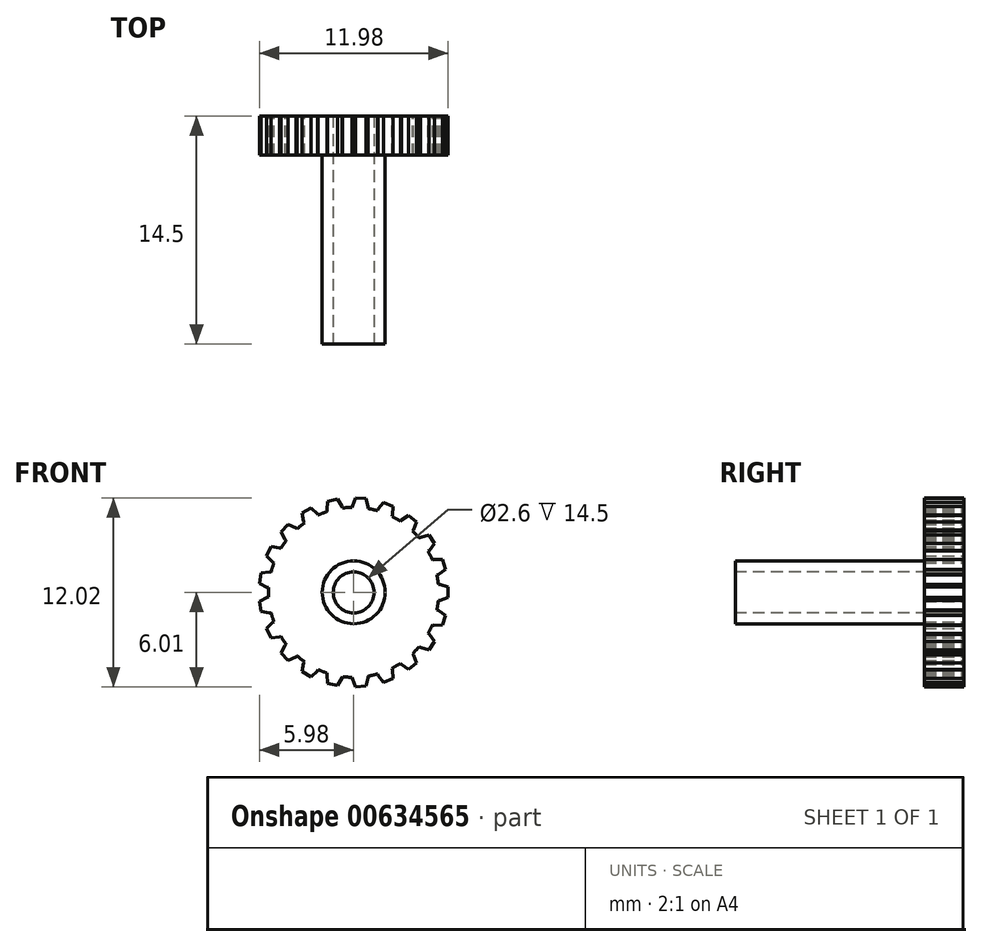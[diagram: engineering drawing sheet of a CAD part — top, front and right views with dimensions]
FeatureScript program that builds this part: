
annotation { "Feature Type Name" : "Feature", "Feature Type Description" : "" }
export const myFeature = defineFeature(function(context is Context, id is Id, definition is map)
    precondition{}
    {
        {
            var Q0;
            Q0=qCreatedBy(makeId("Front.planeOp"),FACE);
            var sketch = newSketch(context, id + "F0", { "sketchPlane" : qUnion([Q0])});
            skCircle(sketch, "E0", {"center": v(0, 0) * mm, "radius": 5.4 * mm});
            skLineSegment(sketch, "E1", {"start": v(0, 0) * mm, "end": v(5.4, 0) * mm, "construction": true});
            skLineSegment(sketch, "E2", {"start": v(5.4, 0) * mm, "end": v(6, 0) * mm, "construction": true});
            skLineSegment(sketch, "E3", {"start": v(6, 0) * mm, "end": v(6, 0.33) * mm});
            skLineSegment(sketch, "E4", {"start": v(5.38, 0.5) * mm, "end": v(5.48, 0.5) * mm});
            skLineSegment(sketch, "E5", {"start": v(5.48, 0.5) * mm, "end": v(6, 0.33) * mm});
            skLineSegment(sketch, "E6.MirrorCS", {"start": v(5.48, -0.5) * mm, "end": v(6, -0.33) * mm});
            skLineSegment(sketch, "E7.MirrorCS", {"start": v(6, 0) * mm, "end": v(6, -0.33) * mm});
            skLineSegment(sketch, "E8.MirrorCS", {"start": v(5.38, -0.5) * mm, "end": v(5.48, -0.5) * mm});
            skLineSegment(sketch, "E9.1.0", {"start": v(5, 2.06) * mm, "end": v(5.09, 2.1) * mm});
            skLineSegment(sketch, "E9.1.1", {"start": v(5.09, 2.1) * mm, "end": v(5.64, 2.08) * mm});
            skLineSegment(sketch, "E9.1.2", {"start": v(5.73, 1.77) * mm, "end": v(5.64, 2.08) * mm});
            skLineSegment(sketch, "E9.1.3", {"start": v(5.73, 1.77) * mm, "end": v(5.83, 1.45) * mm});
            skLineSegment(sketch, "E9.1.4", {"start": v(5.38, 1.14) * mm, "end": v(5.83, 1.45) * mm});
            skLineSegment(sketch, "E9.1.5", {"start": v(5.29, 1.1) * mm, "end": v(5.38, 1.14) * mm});
            skLineSegment(sketch, "E9.2.0", {"start": v(4.16, 3.44) * mm, "end": v(4.24, 3.5) * mm});
            skLineSegment(sketch, "E9.2.1", {"start": v(4.24, 3.5) * mm, "end": v(4.77, 3.65) * mm});
            skLineSegment(sketch, "E9.2.2", {"start": v(4.96, 3.38) * mm, "end": v(4.77, 3.65) * mm});
            skLineSegment(sketch, "E9.2.3", {"start": v(4.96, 3.38) * mm, "end": v(5.14, 3.1) * mm});
            skLineSegment(sketch, "E9.2.4", {"start": v(4.8, 2.67) * mm, "end": v(5.14, 3.1) * mm});
            skLineSegment(sketch, "E9.2.5", {"start": v(4.72, 2.62) * mm, "end": v(4.8, 2.67) * mm});
            skLineSegment(sketch, "E9.3.0", {"start": v(2.96, 4.52) * mm, "end": v(3.02, 4.6) * mm});
            skLineSegment(sketch, "E9.3.1", {"start": v(3.02, 4.6) * mm, "end": v(3.48, 4.9) * mm});
            skLineSegment(sketch, "E9.3.2", {"start": v(3.74, 4.7) * mm, "end": v(3.48, 4.9) * mm});
            skLineSegment(sketch, "E9.3.3", {"start": v(3.74, 4.7) * mm, "end": v(4, 4.49) * mm});
            skLineSegment(sketch, "E9.3.4", {"start": v(3.8, 3.97) * mm, "end": v(4, 4.49) * mm});
            skLineSegment(sketch, "E9.3.5", {"start": v(3.74, 3.9) * mm, "end": v(3.8, 3.97) * mm});
            skLineSegment(sketch, "E9.4.0", {"start": v(1.5, 5.19) * mm, "end": v(1.54, 5.28) * mm});
            skLineSegment(sketch, "E9.4.1", {"start": v(1.54, 5.28) * mm, "end": v(1.88, 5.7) * mm});
            skLineSegment(sketch, "E9.4.2", {"start": v(2.2, 5.59) * mm, "end": v(1.88, 5.7) * mm});
            skLineSegment(sketch, "E9.4.3", {"start": v(2.2, 5.59) * mm, "end": v(2.5, 5.46) * mm});
            skLineSegment(sketch, "E9.4.4", {"start": v(2.47, 4.92) * mm, "end": v(2.5, 5.46) * mm});
            skLineSegment(sketch, "E9.4.5", {"start": v(2.43, 4.82) * mm, "end": v(2.47, 4.92) * mm});
            skLineSegment(sketch, "E9.5.0", {"start": v(-0.1, 5.4) * mm, "end": v(-0.09, 5.5) * mm});
            skLineSegment(sketch, "E9.5.1", {"start": v(-0.09, 5.5) * mm, "end": v(0.12, 6) * mm});
            skLineSegment(sketch, "E9.5.2", {"start": v(0.45, 5.98) * mm, "end": v(0.12, 6) * mm});
            skLineSegment(sketch, "E9.5.3", {"start": v(0.45, 5.98) * mm, "end": v(0.78, 5.96) * mm});
            skLineSegment(sketch, "E9.5.4", {"start": v(0.9, 5.42) * mm, "end": v(0.78, 5.96) * mm});
            skLineSegment(sketch, "E9.5.5", {"start": v(0.9, 5.32) * mm, "end": v(0.9, 5.42) * mm});
            skLineSegment(sketch, "E9.6.0", {"start": v(-1.68, 5.13) * mm, "end": v(-1.7, 5.23) * mm});
            skLineSegment(sketch, "E9.6.1", {"start": v(-1.7, 5.23) * mm, "end": v(-1.66, 5.78) * mm});
            skLineSegment(sketch, "E9.6.2", {"start": v(-1.34, 5.85) * mm, "end": v(-1.66, 5.78) * mm});
            skLineSegment(sketch, "E9.6.3", {"start": v(-1.34, 5.85) * mm, "end": v(-1.01, 5.92) * mm});
            skLineSegment(sketch, "E9.6.4", {"start": v(-0.73, 5.45) * mm, "end": v(-1.01, 5.92) * mm});
            skLineSegment(sketch, "E9.6.5", {"start": v(-0.7, 5.35) * mm, "end": v(-0.73, 5.45) * mm});
            skLineSegment(sketch, "E9.7.0", {"start": v(-3.12, 4.4) * mm, "end": v(-3.17, 4.5) * mm});
            skLineSegment(sketch, "E9.7.1", {"start": v(-3.17, 4.5) * mm, "end": v(-3.29, 5.03) * mm});
            skLineSegment(sketch, "E9.7.2", {"start": v(-3, 5.2) * mm, "end": v(-3.29, 5.03) * mm});
            skLineSegment(sketch, "E9.7.3", {"start": v(-3, 5.2) * mm, "end": v(-2.71, 5.36) * mm});
            skLineSegment(sketch, "E9.7.4", {"start": v(-2.3, 5) * mm, "end": v(-2.71, 5.36) * mm});
            skLineSegment(sketch, "E9.7.5", {"start": v(-2.26, 4.9) * mm, "end": v(-2.3, 5) * mm});
            skLineSegment(sketch, "E9.8.0", {"start": v(-4.28, 3.3) * mm, "end": v(-4.35, 3.36) * mm});
            skLineSegment(sketch, "E9.8.1", {"start": v(-4.35, 3.36) * mm, "end": v(-4.62, 3.84) * mm});
            skLineSegment(sketch, "E9.8.2", {"start": v(-4.4, 4.08) * mm, "end": v(-4.62, 3.84) * mm});
            skLineSegment(sketch, "E9.8.3", {"start": v(-4.4, 4.08) * mm, "end": v(-4.17, 4.32) * mm});
            skLineSegment(sketch, "E9.8.4", {"start": v(-3.67, 4.1) * mm, "end": v(-4.17, 4.32) * mm});
            skLineSegment(sketch, "E9.8.5", {"start": v(-3.6, 4.02) * mm, "end": v(-3.67, 4.1) * mm});
            skLineSegment(sketch, "E9.9.0", {"start": v(-5.06, 1.88) * mm, "end": v(-5.15, 1.93) * mm});
            skLineSegment(sketch, "E9.9.1", {"start": v(-5.15, 1.93) * mm, "end": v(-5.55, 2.3) * mm});
            skLineSegment(sketch, "E9.9.2", {"start": v(-5.4, 2.6) * mm, "end": v(-5.55, 2.3) * mm});
            skLineSegment(sketch, "E9.9.3", {"start": v(-5.4, 2.6) * mm, "end": v(-5.26, 2.9) * mm});
            skLineSegment(sketch, "E9.9.4", {"start": v(-4.72, 2.83) * mm, "end": v(-5.26, 2.9) * mm});
            skLineSegment(sketch, "E9.9.5", {"start": v(-4.63, 2.78) * mm, "end": v(-4.72, 2.83) * mm});
            skLineSegment(sketch, "E9.10.0", {"start": v(-5.4, 0.3) * mm, "end": v(-5.5, 0.32) * mm});
            skLineSegment(sketch, "E9.10.1", {"start": v(-5.5, 0.32) * mm, "end": v(-5.98, 0.57) * mm});
            skLineSegment(sketch, "E9.10.2", {"start": v(-5.93, 0.9) * mm, "end": v(-5.98, 0.57) * mm});
            skLineSegment(sketch, "E9.10.3", {"start": v(-5.93, 0.9) * mm, "end": v(-5.88, 1.22) * mm});
            skLineSegment(sketch, "E9.10.4", {"start": v(-5.34, 1.31) * mm, "end": v(-5.88, 1.22) * mm});
            skLineSegment(sketch, "E9.10.5", {"start": v(-5.24, 1.3) * mm, "end": v(-5.34, 1.31) * mm});
            skLineSegment(sketch, "E9.11.0", {"start": v(-5.24, -1.3) * mm, "end": v(-5.34, -1.31) * mm});
            skLineSegment(sketch, "E9.11.1", {"start": v(-5.34, -1.31) * mm, "end": v(-5.88, -1.22) * mm});
            skLineSegment(sketch, "E9.11.2", {"start": v(-5.93, -0.9) * mm, "end": v(-5.88, -1.22) * mm});
            skLineSegment(sketch, "E9.11.3", {"start": v(-5.93, -0.9) * mm, "end": v(-5.98, -0.57) * mm});
            skLineSegment(sketch, "E9.11.4", {"start": v(-5.5, -0.32) * mm, "end": v(-5.98, -0.57) * mm});
            skLineSegment(sketch, "E9.11.5", {"start": v(-5.4, -0.3) * mm, "end": v(-5.5, -0.32) * mm});
            skLineSegment(sketch, "E9.12.0", {"start": v(-4.63, -2.78) * mm, "end": v(-4.72, -2.83) * mm});
            skLineSegment(sketch, "E9.12.1", {"start": v(-4.72, -2.83) * mm, "end": v(-5.26, -2.9) * mm});
            skLineSegment(sketch, "E9.12.2", {"start": v(-5.4, -2.6) * mm, "end": v(-5.26, -2.9) * mm});
            skLineSegment(sketch, "E9.12.3", {"start": v(-5.4, -2.6) * mm, "end": v(-5.55, -2.3) * mm});
            skLineSegment(sketch, "E9.12.4", {"start": v(-5.15, -1.93) * mm, "end": v(-5.55, -2.3) * mm});
            skLineSegment(sketch, "E9.12.5", {"start": v(-5.06, -1.88) * mm, "end": v(-5.15, -1.93) * mm});
            skLineSegment(sketch, "E9.13.0", {"start": v(-3.6, -4.02) * mm, "end": v(-3.67, -4.1) * mm});
            skLineSegment(sketch, "E9.13.1", {"start": v(-3.67, -4.1) * mm, "end": v(-4.17, -4.32) * mm});
            skLineSegment(sketch, "E9.13.2", {"start": v(-4.4, -4.08) * mm, "end": v(-4.17, -4.32) * mm});
            skLineSegment(sketch, "E9.13.3", {"start": v(-4.4, -4.08) * mm, "end": v(-4.62, -3.84) * mm});
            skLineSegment(sketch, "E9.13.4", {"start": v(-4.35, -3.36) * mm, "end": v(-4.62, -3.84) * mm});
            skLineSegment(sketch, "E9.13.5", {"start": v(-4.28, -3.3) * mm, "end": v(-4.35, -3.36) * mm});
            skLineSegment(sketch, "E9.14.0", {"start": v(-2.26, -4.9) * mm, "end": v(-2.3, -5) * mm});
            skLineSegment(sketch, "E9.14.1", {"start": v(-2.3, -5) * mm, "end": v(-2.71, -5.36) * mm});
            skLineSegment(sketch, "E9.14.2", {"start": v(-3, -5.2) * mm, "end": v(-2.71, -5.36) * mm});
            skLineSegment(sketch, "E9.14.3", {"start": v(-3, -5.2) * mm, "end": v(-3.29, -5.03) * mm});
            skLineSegment(sketch, "E9.14.4", {"start": v(-3.17, -4.5) * mm, "end": v(-3.29, -5.03) * mm});
            skLineSegment(sketch, "E9.14.5", {"start": v(-3.12, -4.4) * mm, "end": v(-3.17, -4.5) * mm});
            skLineSegment(sketch, "E9.15.0", {"start": v(-0.7, -5.35) * mm, "end": v(-0.73, -5.45) * mm});
            skLineSegment(sketch, "E9.15.1", {"start": v(-0.73, -5.45) * mm, "end": v(-1.01, -5.92) * mm});
            skLineSegment(sketch, "E9.15.2", {"start": v(-1.34, -5.85) * mm, "end": v(-1.01, -5.92) * mm});
            skLineSegment(sketch, "E9.15.3", {"start": v(-1.34, -5.85) * mm, "end": v(-1.66, -5.78) * mm});
            skLineSegment(sketch, "E9.15.4", {"start": v(-1.7, -5.23) * mm, "end": v(-1.66, -5.78) * mm});
            skLineSegment(sketch, "E9.15.5", {"start": v(-1.68, -5.13) * mm, "end": v(-1.7, -5.23) * mm});
            skLineSegment(sketch, "E9.16.0", {"start": v(0.9, -5.32) * mm, "end": v(0.9, -5.42) * mm});
            skLineSegment(sketch, "E9.16.1", {"start": v(0.9, -5.42) * mm, "end": v(0.78, -5.96) * mm});
            skLineSegment(sketch, "E9.16.2", {"start": v(0.45, -5.98) * mm, "end": v(0.78, -5.96) * mm});
            skLineSegment(sketch, "E9.16.3", {"start": v(0.45, -5.98) * mm, "end": v(0.12, -6) * mm});
            skLineSegment(sketch, "E9.16.4", {"start": v(-0.09, -5.5) * mm, "end": v(0.12, -6) * mm});
            skLineSegment(sketch, "E9.16.5", {"start": v(-0.1, -5.4) * mm, "end": v(-0.09, -5.5) * mm});
            skLineSegment(sketch, "E9.17.0", {"start": v(2.43, -4.82) * mm, "end": v(2.47, -4.92) * mm});
            skLineSegment(sketch, "E9.17.1", {"start": v(2.47, -4.92) * mm, "end": v(2.5, -5.46) * mm});
            skLineSegment(sketch, "E9.17.2", {"start": v(2.2, -5.59) * mm, "end": v(2.5, -5.46) * mm});
            skLineSegment(sketch, "E9.17.3", {"start": v(2.2, -5.59) * mm, "end": v(1.88, -5.7) * mm});
            skLineSegment(sketch, "E9.17.4", {"start": v(1.54, -5.28) * mm, "end": v(1.88, -5.7) * mm});
            skLineSegment(sketch, "E9.17.5", {"start": v(1.5, -5.19) * mm, "end": v(1.54, -5.28) * mm});
            skLineSegment(sketch, "E9.18.0", {"start": v(3.74, -3.9) * mm, "end": v(3.8, -3.97) * mm});
            skLineSegment(sketch, "E9.18.1", {"start": v(3.8, -3.97) * mm, "end": v(4, -4.49) * mm});
            skLineSegment(sketch, "E9.18.2", {"start": v(3.74, -4.7) * mm, "end": v(4, -4.49) * mm});
            skLineSegment(sketch, "E9.18.3", {"start": v(3.74, -4.7) * mm, "end": v(3.48, -4.9) * mm});
            skLineSegment(sketch, "E9.18.4", {"start": v(3.02, -4.6) * mm, "end": v(3.48, -4.9) * mm});
            skLineSegment(sketch, "E9.18.5", {"start": v(2.96, -4.52) * mm, "end": v(3.02, -4.6) * mm});
            skLineSegment(sketch, "E9.19.0", {"start": v(4.72, -2.62) * mm, "end": v(4.8, -2.67) * mm});
            skLineSegment(sketch, "E9.19.1", {"start": v(4.8, -2.67) * mm, "end": v(5.14, -3.1) * mm});
            skLineSegment(sketch, "E9.19.2", {"start": v(4.96, -3.38) * mm, "end": v(5.14, -3.1) * mm});
            skLineSegment(sketch, "E9.19.3", {"start": v(4.96, -3.38) * mm, "end": v(4.77, -3.65) * mm});
            skLineSegment(sketch, "E9.19.4", {"start": v(4.24, -3.5) * mm, "end": v(4.77, -3.65) * mm});
            skLineSegment(sketch, "E9.19.5", {"start": v(4.16, -3.44) * mm, "end": v(4.24, -3.5) * mm});
            skLineSegment(sketch, "E9.20.0", {"start": v(5.29, -1.1) * mm, "end": v(5.38, -1.14) * mm});
            skLineSegment(sketch, "E9.20.1", {"start": v(5.38, -1.14) * mm, "end": v(5.83, -1.45) * mm});
            skLineSegment(sketch, "E9.20.2", {"start": v(5.73, -1.77) * mm, "end": v(5.83, -1.45) * mm});
            skLineSegment(sketch, "E9.20.3", {"start": v(5.73, -1.77) * mm, "end": v(5.64, -2.08) * mm});
            skLineSegment(sketch, "E9.20.4", {"start": v(5.09, -2.1) * mm, "end": v(5.64, -2.08) * mm});
            skLineSegment(sketch, "E9.20.5", {"start": v(5, -2.06) * mm, "end": v(5.09, -2.1) * mm});
            skSolve(sketch);
        }
        {
            var Q0;
            Q0=qSketchRegion(id+"F0",true);
            extrude(context, id + "F1", {"entities" : qUnion([Q0]), "depth" : 2.5 * mm, "offsetDistance" : 25.4 * mm});
        }
        {
            var Q0;
            Q0=makeQuery(id+"F1.opExtrude","CAP_FACE",FACE,{"disambiguationData":[OSD([sQuery(id+"F0.wireOp",EDGE,"E0"),sQuery(id+"F0.wireOp",EDGE,"E3"),sQuery(id+"F0.wireOp",EDGE,"E4"),sQuery(id+"F0.wireOp",EDGE,"E5"),sQuery(id+"F0.wireOp",EDGE,"E6.MirrorCS"),sQuery(id+"F0.wireOp",EDGE,"E7.MirrorCS"),sQuery(id+"F0.wireOp",EDGE,"E8.MirrorCS"),sQuery(id+"F0.wireOp",EDGE,"E9.1.0"),sQuery(id+"F0.wireOp",EDGE,"E9.1.1"),sQuery(id+"F0.wireOp",EDGE,"E9.1.2"),sQuery(id+"F0.wireOp",EDGE,"E9.1.3"),sQuery(id+"F0.wireOp",EDGE,"E9.1.4"),sQuery(id+"F0.wireOp",EDGE,"E9.1.5"),sQuery(id+"F0.wireOp",EDGE,"E9.2.0"),sQuery(id+"F0.wireOp",EDGE,"E9.2.1"),sQuery(id+"F0.wireOp",EDGE,"E9.2.2"),sQuery(id+"F0.wireOp",EDGE,"E9.2.3"),sQuery(id+"F0.wireOp",EDGE,"E9.2.4"),sQuery(id+"F0.wireOp",EDGE,"E9.2.5"),sQuery(id+"F0.wireOp",EDGE,"E9.3.0"),sQuery(id+"F0.wireOp",EDGE,"E9.3.1"),sQuery(id+"F0.wireOp",EDGE,"E9.3.2"),sQuery(id+"F0.wireOp",EDGE,"E9.3.3"),sQuery(id+"F0.wireOp",EDGE,"E9.3.4"),sQuery(id+"F0.wireOp",EDGE,"E9.3.5"),sQuery(id+"F0.wireOp",EDGE,"E9.4.0"),sQuery(id+"F0.wireOp",EDGE,"E9.4.1"),sQuery(id+"F0.wireOp",EDGE,"E9.4.2"),sQuery(id+"F0.wireOp",EDGE,"E9.4.3"),sQuery(id+"F0.wireOp",EDGE,"E9.4.4"),sQuery(id+"F0.wireOp",EDGE,"E9.4.5"),sQuery(id+"F0.wireOp",EDGE,"E9.5.0"),sQuery(id+"F0.wireOp",EDGE,"E9.5.1"),sQuery(id+"F0.wireOp",EDGE,"E9.5.2"),sQuery(id+"F0.wireOp",EDGE,"E9.5.3"),sQuery(id+"F0.wireOp",EDGE,"E9.5.4"),sQuery(id+"F0.wireOp",EDGE,"E9.5.5"),sQuery(id+"F0.wireOp",EDGE,"E9.6.0"),sQuery(id+"F0.wireOp",EDGE,"E9.6.1"),sQuery(id+"F0.wireOp",EDGE,"E9.6.2"),sQuery(id+"F0.wireOp",EDGE,"E9.6.3"),sQuery(id+"F0.wireOp",EDGE,"E9.6.4"),sQuery(id+"F0.wireOp",EDGE,"E9.6.5"),sQuery(id+"F0.wireOp",EDGE,"E9.7.0"),sQuery(id+"F0.wireOp",EDGE,"E9.7.1"),sQuery(id+"F0.wireOp",EDGE,"E9.7.2"),sQuery(id+"F0.wireOp",EDGE,"E9.7.3"),sQuery(id+"F0.wireOp",EDGE,"E9.7.4"),sQuery(id+"F0.wireOp",EDGE,"E9.7.5"),sQuery(id+"F0.wireOp",EDGE,"E9.8.0"),sQuery(id+"F0.wireOp",EDGE,"E9.8.1"),sQuery(id+"F0.wireOp",EDGE,"E9.8.2"),sQuery(id+"F0.wireOp",EDGE,"E9.8.3"),sQuery(id+"F0.wireOp",EDGE,"E9.8.4"),sQuery(id+"F0.wireOp",EDGE,"E9.8.5"),sQuery(id+"F0.wireOp",EDGE,"E9.9.0"),sQuery(id+"F0.wireOp",EDGE,"E9.9.1"),sQuery(id+"F0.wireOp",EDGE,"E9.9.2"),sQuery(id+"F0.wireOp",EDGE,"E9.9.3"),sQuery(id+"F0.wireOp",EDGE,"E9.9.4"),sQuery(id+"F0.wireOp",EDGE,"E9.9.5"),sQuery(id+"F0.wireOp",EDGE,"E9.10.0"),sQuery(id+"F0.wireOp",EDGE,"E9.10.1"),sQuery(id+"F0.wireOp",EDGE,"E9.10.2"),sQuery(id+"F0.wireOp",EDGE,"E9.10.3"),sQuery(id+"F0.wireOp",EDGE,"E9.10.4"),sQuery(id+"F0.wireOp",EDGE,"E9.10.5"),sQuery(id+"F0.wireOp",EDGE,"E9.11.0"),sQuery(id+"F0.wireOp",EDGE,"E9.11.1"),sQuery(id+"F0.wireOp",EDGE,"E9.11.2"),sQuery(id+"F0.wireOp",EDGE,"E9.11.3"),sQuery(id+"F0.wireOp",EDGE,"E9.11.4"),sQuery(id+"F0.wireOp",EDGE,"E9.11.5"),sQuery(id+"F0.wireOp",EDGE,"E9.12.0"),sQuery(id+"F0.wireOp",EDGE,"E9.12.1"),sQuery(id+"F0.wireOp",EDGE,"E9.12.2"),sQuery(id+"F0.wireOp",EDGE,"E9.12.3"),sQuery(id+"F0.wireOp",EDGE,"E9.12.4"),sQuery(id+"F0.wireOp",EDGE,"E9.12.5"),sQuery(id+"F0.wireOp",EDGE,"E9.13.0"),sQuery(id+"F0.wireOp",EDGE,"E9.13.1"),sQuery(id+"F0.wireOp",EDGE,"E9.13.2"),sQuery(id+"F0.wireOp",EDGE,"E9.13.3"),sQuery(id+"F0.wireOp",EDGE,"E9.13.4"),sQuery(id+"F0.wireOp",EDGE,"E9.13.5"),sQuery(id+"F0.wireOp",EDGE,"E9.14.0"),sQuery(id+"F0.wireOp",EDGE,"E9.14.1"),sQuery(id+"F0.wireOp",EDGE,"E9.14.2"),sQuery(id+"F0.wireOp",EDGE,"E9.14.3"),sQuery(id+"F0.wireOp",EDGE,"E9.14.4"),sQuery(id+"F0.wireOp",EDGE,"E9.14.5"),sQuery(id+"F0.wireOp",EDGE,"E9.15.0"),sQuery(id+"F0.wireOp",EDGE,"E9.15.1"),sQuery(id+"F0.wireOp",EDGE,"E9.15.2"),sQuery(id+"F0.wireOp",EDGE,"E9.15.3"),sQuery(id+"F0.wireOp",EDGE,"E9.15.4"),sQuery(id+"F0.wireOp",EDGE,"E9.15.5"),sQuery(id+"F0.wireOp",EDGE,"E9.16.0"),sQuery(id+"F0.wireOp",EDGE,"E9.16.1"),sQuery(id+"F0.wireOp",EDGE,"E9.16.2"),sQuery(id+"F0.wireOp",EDGE,"E9.16.3"),sQuery(id+"F0.wireOp",EDGE,"E9.16.4"),sQuery(id+"F0.wireOp",EDGE,"E9.16.5"),sQuery(id+"F0.wireOp",EDGE,"E9.17.0"),sQuery(id+"F0.wireOp",EDGE,"E9.17.1"),sQuery(id+"F0.wireOp",EDGE,"E9.17.2"),sQuery(id+"F0.wireOp",EDGE,"E9.17.3"),sQuery(id+"F0.wireOp",EDGE,"E9.17.4"),sQuery(id+"F0.wireOp",EDGE,"E9.17.5"),sQuery(id+"F0.wireOp",EDGE,"E9.18.0"),sQuery(id+"F0.wireOp",EDGE,"E9.18.1"),sQuery(id+"F0.wireOp",EDGE,"E9.18.2"),sQuery(id+"F0.wireOp",EDGE,"E9.18.3"),sQuery(id+"F0.wireOp",EDGE,"E9.18.4"),sQuery(id+"F0.wireOp",EDGE,"E9.18.5"),sQuery(id+"F0.wireOp",EDGE,"E9.19.0"),sQuery(id+"F0.wireOp",EDGE,"E9.19.1"),sQuery(id+"F0.wireOp",EDGE,"E9.19.2"),sQuery(id+"F0.wireOp",EDGE,"E9.19.3"),sQuery(id+"F0.wireOp",EDGE,"E9.19.4"),sQuery(id+"F0.wireOp",EDGE,"E9.19.5"),sQuery(id+"F0.wireOp",EDGE,"E9.20.0"),sQuery(id+"F0.wireOp",EDGE,"E9.20.1"),sQuery(id+"F0.wireOp",EDGE,"E9.20.2"),sQuery(id+"F0.wireOp",EDGE,"E9.20.3"),sQuery(id+"F0.wireOp",EDGE,"E9.20.4"),sQuery(id+"F0.wireOp",EDGE,"E9.20.5")])],"isStart":false});
            var sketch = newSketch(context, id + "F2", { "sketchPlane" : qUnion([Q0])});
            skCircle(sketch, "E10", {"center": v(0, 0) * mm, "radius": 2 * mm});
            skSolve(sketch);
        }
        {
            var Q0;
            Q0=qSketchRegion(id+"F2",true);
            extrude(context, id + "F3", {"entities" : qUnion([Q0]), "operationType" : NewBodyOperationType.ADD, "depth" : 12 * mm, "offsetDistance" : 25.4 * mm});
        }
        {
            var Q0;
            Q0=makeQuery(id+"F3.opExtrude","CAP_FACE",FACE,{"disambiguationData":[OSD([sQuery(id+"F2.wireOp",EDGE,"E10")])],"isStart":false});
            var sketch = newSketch(context, id + "F4", { "sketchPlane" : qUnion([Q0])});
            skCircle(sketch, "E11", {"center": v(0, 0) * mm, "radius": 1.3 * mm});
            skSolve(sketch);
        }
        {
            var Q0;
            Q0=qSketchRegion(id+"F4",true);
            extrude(context, id + "F5", {"entities" : qUnion([Q0]), "operationType" : NewBodyOperationType.REMOVE, "oppositeDirection" : true, "depth" : 25.25 * mm, "offsetDistance" : 25.4 * mm});
        }
    });
